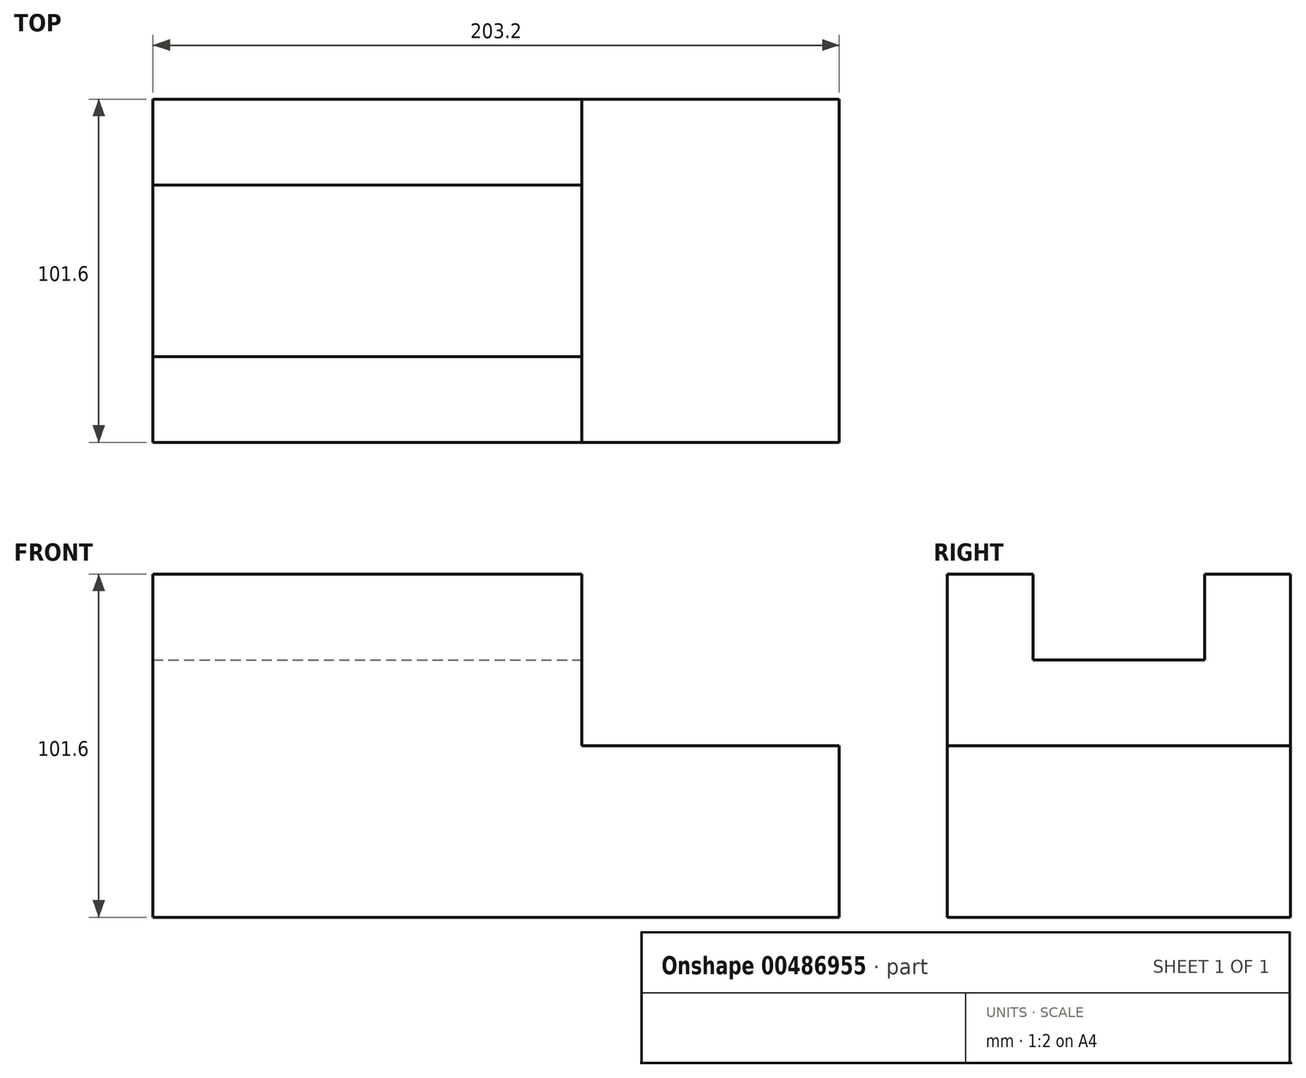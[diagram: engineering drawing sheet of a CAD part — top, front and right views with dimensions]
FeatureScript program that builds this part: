
annotation { "Feature Type Name" : "Feature", "Feature Type Description" : "" }
export const myFeature = defineFeature(function(context is Context, id is Id, definition is map)
    precondition{}
    {
        {
            var Q0;
            Q0=qCreatedBy(makeId("Front.planeOp"),FACE);
            var sketch = newSketch(context, id + "F0", { "sketchPlane" : qUnion([Q0])});
            skLineSegment(sketch, "E0.bottom", {"start": v(-127, 101.6) * mm, "end": v(0, 101.6) * mm});
            skLineSegment(sketch, "E0.top", {"start": v(-127, 0) * mm, "end": v(0, 0) * mm});
            skLineSegment(sketch, "E0.left", {"start": v(-127, 101.6) * mm, "end": v(-127, 0) * mm});
            skLineSegment(sketch, "E1.bottom", {"start": v(0, 0) * mm, "end": v(76.2, 0) * mm});
            skLineSegment(sketch, "E1.top", {"start": v(0, 50.8) * mm, "end": v(76.2, 50.8) * mm});
            skLineSegment(sketch, "E1.right", {"start": v(76.2, 0) * mm, "end": v(76.2, 50.8) * mm});
            skLineSegment(sketch, "E2", {"start": v(0, 101.6) * mm, "end": v(0, 50.8) * mm});
            skSolve(sketch);
        }
        {
            var Q0;
            Q0 = qSketchRegion(id + "F0", true);
            extrude(context, id + "F1", {"entities" : qUnion([Q0]), "depth" : 101.6 * mm});
        }
        {
            var Q0;
            Q0=makeQuery(id+"F1.opExtrude","SWEPT_FACE",FACE,{"disambiguationData":[OSD([sQuery(id+"F0.wireOp",EDGE,"E0.bottom")])]});
            var sketch = newSketch(context, id + "F2", { "sketchPlane" : qUnion([Q0])});
            skLineSegment(sketch, "E3.bottom", {"start": v(-127, -25.4) * mm, "end": v(0, -25.4) * mm});
            skLineSegment(sketch, "E3.top", {"start": v(-127, -76.2) * mm, "end": v(0, -76.2) * mm});
            skLineSegment(sketch, "E3.left", {"start": v(-127, -25.4) * mm, "end": v(-127, -76.2) * mm});
            skLineSegment(sketch, "E3.right", {"start": v(0, -25.4) * mm, "end": v(0, -76.2) * mm});
            skSolve(sketch);
        }
        {
            var Q0;
            Q0 = qSketchRegion(id + "F2", true);
            extrude(context, id + "F3", {"entities" : qUnion([Q0]), "operationType" : NewBodyOperationType.REMOVE, "oppositeDirection" : true, "depth" : 25.4 * mm});
        }
    });
